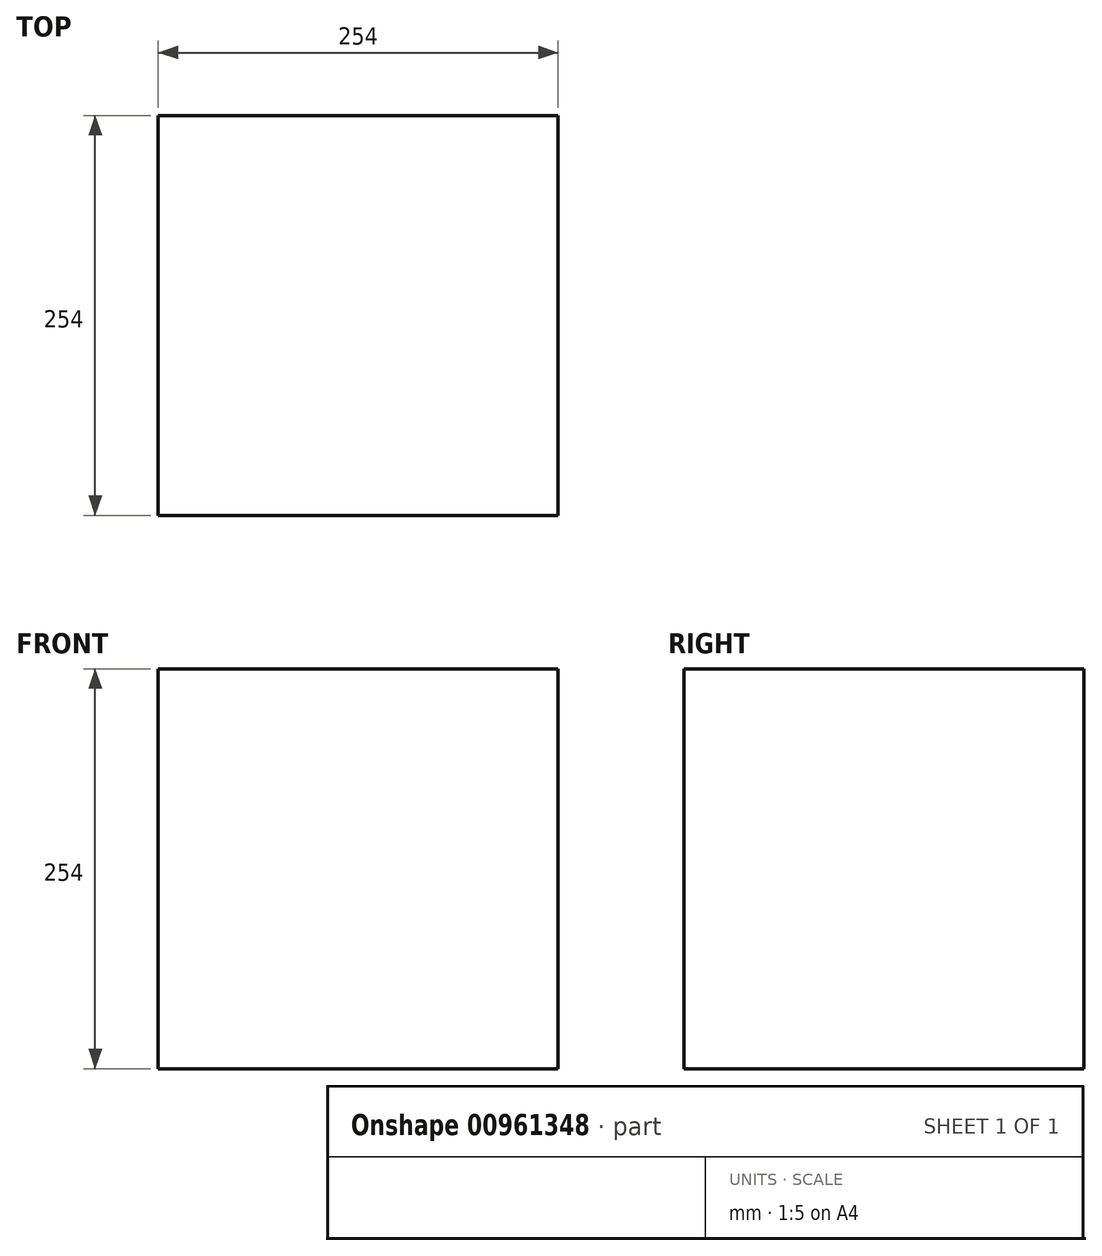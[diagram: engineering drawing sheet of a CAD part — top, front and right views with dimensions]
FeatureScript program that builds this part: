
annotation { "Feature Type Name" : "Feature", "Feature Type Description" : "" }
export const myFeature = defineFeature(function(context is Context, id is Id, definition is map)
    precondition{}
    {
        {
            var Q0;
            Q0=qCreatedBy(makeId("Front.planeOp"),FACE);
            var sketch = newSketch(context, id + "F0", { "sketchPlane" : qUnion([Q0])});
            skLineSegment(sketch, "E0.bottom", {"start": v(-127, 127) * mm, "end": v(127, 127) * mm});
            skLineSegment(sketch, "E0.top", {"start": v(-127, -127) * mm, "end": v(127, -127) * mm});
            skLineSegment(sketch, "E0.left", {"start": v(-127, 127) * mm, "end": v(-127, -127) * mm});
            skLineSegment(sketch, "E0.right", {"start": v(127, 127) * mm, "end": v(127, -127) * mm});
            skPoint(sketch, "E0.middle", {"position": v(0, 0) * mm});
            skSolve(sketch);
        }
        {
            var Q0;
            Q0=makeQuery(id+"F0.imprint","IMPRINT",FACE,{"disambiguationData":[TD([[makeQuery(id+"F0.imprint","IMPRINT",EDGE,{"derivedFrom":sQuery(id+"F0.wireOp",EDGE,"E0.bottom")}),-1.0]])]});
            extrude(context, id + "F1", {"entities" : qUnion([Q0]), "depth" : 254 * mm, "offsetDistance" : 25.4 * mm});
        }
    });
